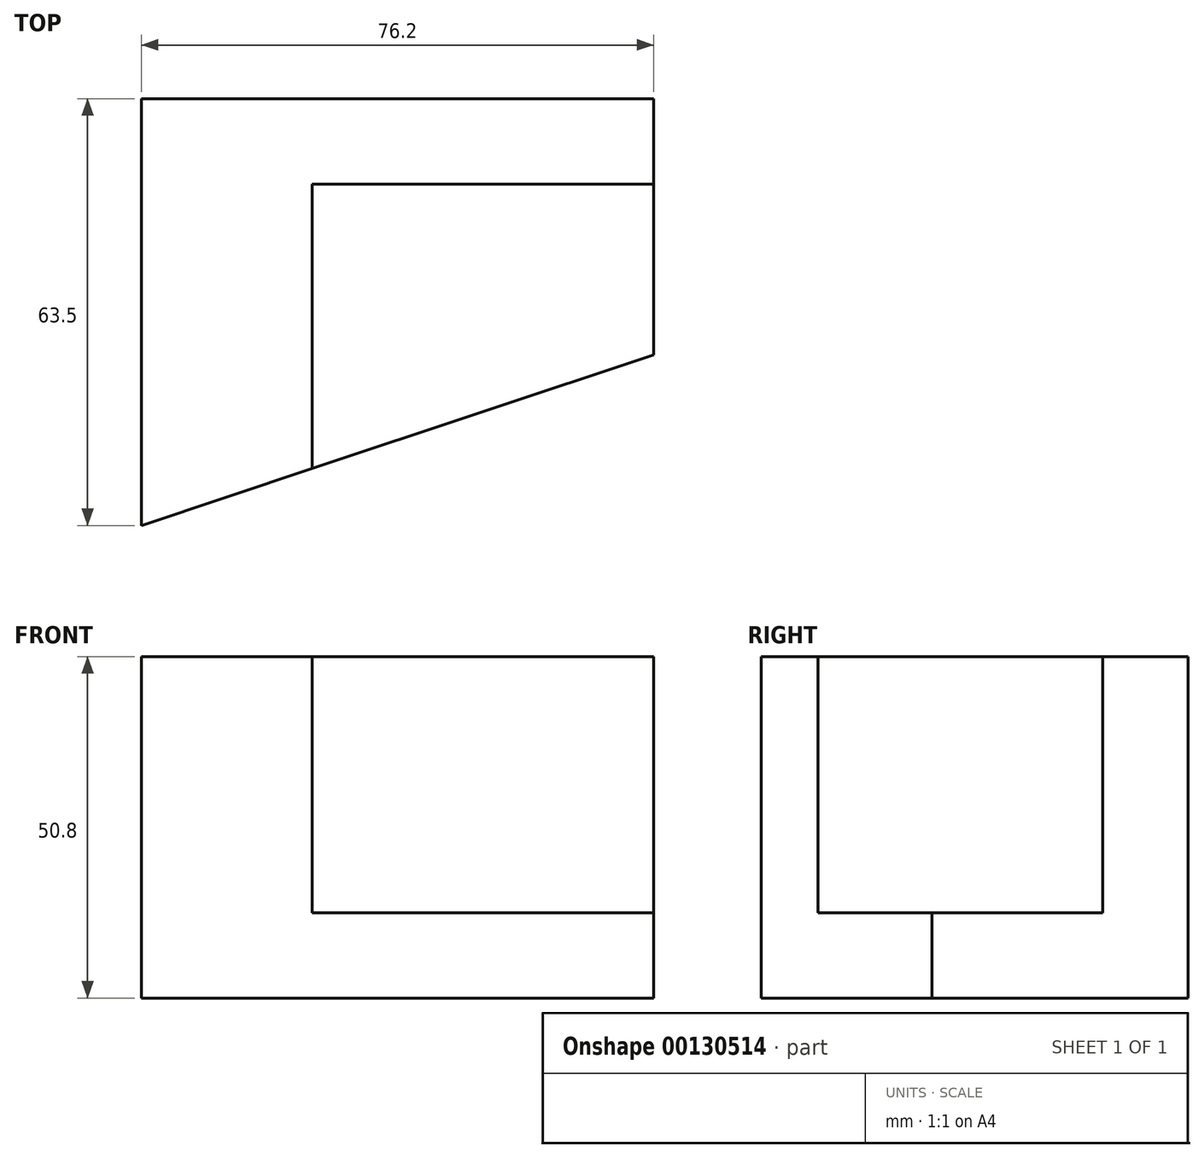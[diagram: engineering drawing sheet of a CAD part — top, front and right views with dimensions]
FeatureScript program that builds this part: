
annotation { "Feature Type Name" : "Feature", "Feature Type Description" : "" }
export const myFeature = defineFeature(function(context is Context, id is Id, definition is map)
    precondition{}
    {
        {
            var Q0;
            Q0=qCreatedBy(makeId("Front.planeOp"),FACE);
            var sketch = newSketch(context, id + "F0", { "sketchPlane" : qUnion([Q0])});
            skLineSegment(sketch, "E0.bottom", {"start": v(0, 0) * mm, "end": v(76.2, 0) * mm});
            skLineSegment(sketch, "E0.top", {"start": v(0, 50.8) * mm, "end": v(76.2, 50.8) * mm});
            skLineSegment(sketch, "E0.left", {"start": v(0, 0) * mm, "end": v(0, 50.8) * mm});
            skLineSegment(sketch, "E0.right", {"start": v(76.2, 0) * mm, "end": v(76.2, 50.8) * mm});
            skLineSegment(sketch, "E1.top", {"start": v(76.2, 12.7) * mm, "end": v(25.4, 12.7) * mm});
            skLineSegment(sketch, "E1.right", {"start": v(25.4, 50.8) * mm, "end": v(25.4, 12.7) * mm});
            skSolve(sketch);
        }
        {
            var Q0;
            {var subQ1=sQuery(id+"F0.wireOp",EDGE,"E0.bottom");Q0=makeQuery(id+"F0.imprint","IMPRINT",FACE,{"disambiguationData":[TD([[makeQuery(id+"F0.imprint","IMPRINT",EDGE,{"derivedFrom":subQ1}),1.0]])]});}
            extrude(context, id + "F1", {"entities" : qUnion([Q0]), "depth" : 50.8 * mm});
        }
        {
            var Q0;
            Q0=makeQuery(id+"F1.opExtrude","CAP_FACE",FACE,{"disambiguationData":[OSD([sQuery(id+"F0.wireOp",EDGE,"E0.bottom"),sQuery(id+"F0.wireOp",EDGE,"E0.top"),sQuery(id+"F0.wireOp",EDGE,"E0.left"),sQuery(id+"F0.wireOp",EDGE,"E0.right"),sQuery(id+"F0.wireOp",EDGE,"E1.top"),sQuery(id+"F0.wireOp",EDGE,"E1.right")])],"isStart":true});
            var sketch = newSketch(context, id + "F2", { "sketchPlane" : qUnion([Q0])});
            skLineSegment(sketch, "E2.bottom", {"start": v(0, 0) * mm, "end": v(-76.2, 0) * mm});
            skLineSegment(sketch, "E2.top", {"start": v(0, 50.8) * mm, "end": v(-76.2, 50.8) * mm});
            skLineSegment(sketch, "E2.left", {"start": v(0, 0) * mm, "end": v(0, 50.8) * mm});
            skLineSegment(sketch, "E2.right", {"start": v(-76.2, 0) * mm, "end": v(-76.2, 50.8) * mm});
            skSolve(sketch);
        }
        {
            var Q0;
            {var subQ4=makeQuery(id+"F1.opExtrude","CAP_EDGE",EDGE,{"disambiguationData":[OSD([sQuery(id+"F0.wireOp",EDGE,"E1.top")])],"isStart":true});Q0=makeQuery(id+"F2.imprint","IMPRINT",FACE,{"disambiguationData":[TD([[makeQuery(id+"F2.imprint","IMPRINT",EDGE,{"derivedFrom":subQ4}),1.0]])]});}
            var Q1;
            {var subQ1=sQuery(id+"F2.wireOp",EDGE,"E2.bottom");Q1=makeQuery(id+"F2.imprint","IMPRINT",FACE,{"disambiguationData":[TD([[makeQuery(id+"F2.imprint","IMPRINT",EDGE,{"derivedFrom":subQ1}),-1.0]])]});}
            extrude(context, id + "F3", {"entities" : qUnion([Q0, Q1]), "operationType" : NewBodyOperationType.ADD, "depth" : 12.7 * mm});
        }
        {
            var Q0;
            Q0=makeQuery(id+"F3.boolean.opBoolean","MERGE",FACE,{"derivedFrom":[makeQuery(id+"F1.opExtrude","SWEPT_FACE",FACE,{"disambiguationData":[OSD([sQuery(id+"F0.wireOp",EDGE,"E0.bottom")])]}),makeQuery(id+"F3.opExtrude","SWEPT_FACE",FACE,{"disambiguationData":[OSD([sQuery(id+"F2.wireOp",EDGE,"E2.bottom")])]})]});
            var sketch = newSketch(context, id + "F4", { "sketchPlane" : qUnion([Q0])});
            skLineSegment(sketch, "E3.0", {"start": v(76.2, 25.4) * mm, "end": v(76.2, -12.7) * mm});
            skLineSegment(sketch, "E3.1", {"start": v(0, 50.8) * mm, "end": v(76.2, 50.8) * mm});
            skLineSegment(sketch, "E3.2", {"start": v(0, -12.7) * mm, "end": v(76.2, -12.7) * mm});
            skLineSegment(sketch, "E3.3", {"start": v(0, 50.8) * mm, "end": v(0, -12.7) * mm});
            skLineSegment(sketch, "E4", {"start": v(0, 50.8) * mm, "end": v(76.2, 25.4) * mm});
            skSolve(sketch);
        }
        {
            var Q0;
            {var subQ0=sQuery(id+"F4.wireOp",EDGE,"E3.1");Q0=makeQuery(id+"F4.imprint","IMPRINT",FACE,{"disambiguationData":[TD([[makeQuery(id+"F4.imprint","IMPRINT",EDGE,{"derivedFrom":subQ0}),-1.0]])]});}
            extrude(context, id + "F5", {"entities" : qUnion([Q0]), "operationType" : NewBodyOperationType.REMOVE, "endBound" : BoundingType.THROUGH_ALL, "oppositeDirection" : true, "depth" : 25.4 * mm});
        }
    });
